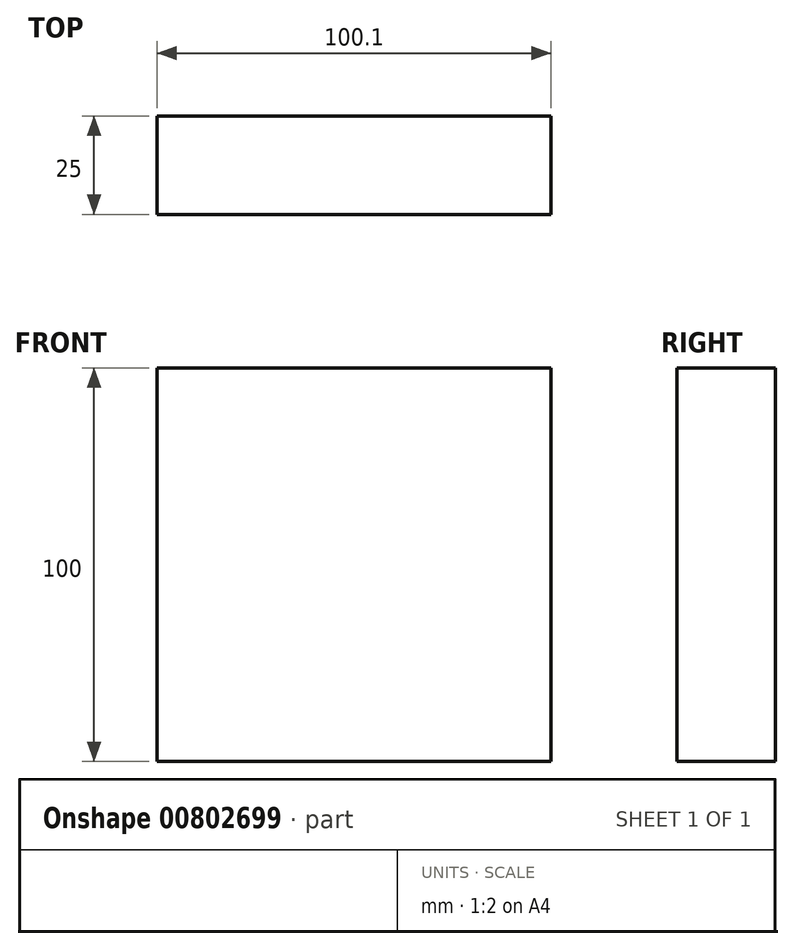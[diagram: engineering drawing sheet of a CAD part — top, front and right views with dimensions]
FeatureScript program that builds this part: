
annotation { "Feature Type Name" : "Feature", "Feature Type Description" : "" }
export const myFeature = defineFeature(function(context is Context, id is Id, definition is map)
    precondition{}
    {
        {
            var Q0;
            Q0=qCreatedBy(makeId("Top.planeOp"),FACE);
            var sketch = newSketch(context, id + "F0", { "sketchPlane" : qUnion([Q0])});
            skLineSegment(sketch, "E0.bottom", {"start": v(50.05, 50.2) * mm, "end": v(-50.05, 50.2) * mm});
            skLineSegment(sketch, "E0.top", {"start": v(50.05, -50.2) * mm, "end": v(-50.05, -50.2) * mm});
            skLineSegment(sketch, "E0.left", {"start": v(50.05, 50.2) * mm, "end": v(50.05, -50.2) * mm});
            skLineSegment(sketch, "E0.right", {"start": v(-50.05, 50.2) * mm, "end": v(-50.05, -50.2) * mm});
            skPoint(sketch, "E0.middle", {"position": v(0, 0) * mm});
            skSolve(sketch);
        }
        {
            var Q0;
            Q0=sQuery(id+"F0.wireOp",EDGE,"E0.top");
            var Q1;
            Q1=sQuery(id+"F0.wireOp",EDGE,"E0.bottom");
            var Q2;
            Q2=sQuery(id+"F0.wireOp",EDGE,"E0.right");
            var Q3;
            Q3=sQuery(id+"F0.wireOp",EDGE,"E0.left");
            extrude(context, id + "F1", {"bodyType" : ToolBodyType.SURFACE, "surfaceEntities" : qUnion([Q0, Q1, Q2, Q3]), "depth" : 100 * mm, "offsetDistance" : 25 * mm});
        }
        {
            var Q0;
            Q0=makeQuery(id+"F1.opExtrude","SWEPT_FACE",FACE,{"disambiguationData":[OSD([sQuery(id+"F0.wireOp",EDGE,"E0.bottom")])]});
            extrude(context, id + "F2", {"entities" : qUnion([Q0]), "depth" : 25 * mm, "offsetDistance" : 25 * mm});
        }
    });
